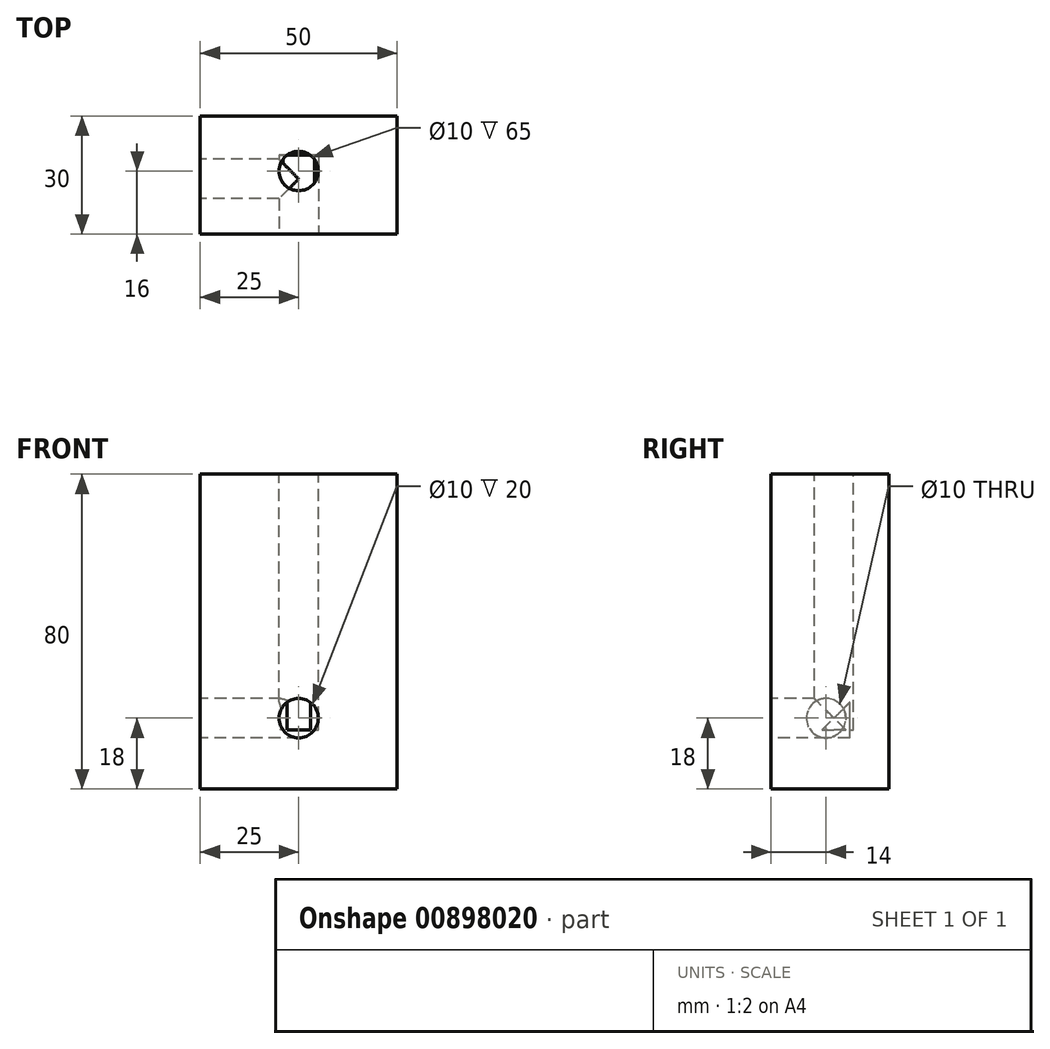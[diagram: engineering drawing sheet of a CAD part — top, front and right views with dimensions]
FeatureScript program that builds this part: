
annotation { "Feature Type Name" : "Feature", "Feature Type Description" : "" }
export const myFeature = defineFeature(function(context is Context, id is Id, definition is map)
    precondition{}
    {
        {
            var Q0;
            Q0=qCreatedBy(makeId("Front.planeOp"),FACE);
            var sketch = newSketch(context, id + "F0", { "sketchPlane" : qUnion([Q0])});
            skLineSegment(sketch, "E0.bottom", {"start": v(-25, 80) * mm, "end": v(25, 80) * mm});
            skLineSegment(sketch, "E0.top", {"start": v(-25, 0) * mm, "end": v(25, 0) * mm});
            skLineSegment(sketch, "E0.left", {"start": v(-25, 80) * mm, "end": v(-25, 0) * mm});
            skLineSegment(sketch, "E0.right", {"start": v(25, 80) * mm, "end": v(25, 0) * mm});
            skSolve(sketch);
        }
        {
            var Q0;
            Q0=makeQuery(id+"F0.imprint","IMPRINT",FACE,{"disambiguationData":[TD([[makeQuery(id+"F0.imprint","IMPRINT",EDGE,{"derivedFrom":sQuery(id+"F0.wireOp",EDGE,"E0.bottom")}),-1.0]])]});
            extrude(context, id + "F1", {"entities" : qUnion([Q0]), "depth" : 30 * mm, "offsetDistance" : 25 * mm});
        }
        {
            var Q0;
            Q0=makeQuery(id+"F1.opExtrude","CAP_FACE",FACE,{"disambiguationData":[OSD([sQuery(id+"F0.wireOp",EDGE,"E0.bottom"),sQuery(id+"F0.wireOp",EDGE,"E0.top"),sQuery(id+"F0.wireOp",EDGE,"E0.left"),sQuery(id+"F0.wireOp",EDGE,"E0.right")])],"isStart":false});
            var sketch = newSketch(context, id + "F2", { "sketchPlane" : qUnion([Q0])});
            skCircle(sketch, "E1", {"center": v(0, 18) * mm, "radius": 5 * mm});
            skSolve(sketch);
        }
        {
            var Q0;
            Q0=makeQuery(id+"F2.imprint","IMPRINT",FACE,{"disambiguationData":[TD([[makeQuery(id+"F2.imprint","IMPRINT",EDGE,{"derivedFrom":sQuery(id+"F2.wireOp",EDGE,"E1")}),1.0]])]});
            extrude(context, id + "F3", {"entities" : qUnion([Q0]), "operationType" : NewBodyOperationType.REMOVE, "oppositeDirection" : true, "depth" : 20 * mm, "offsetDistance" : 25 * mm});
        }
        {
            var Q0;
            Q0=makeQuery(id+"F1.opExtrude","SWEPT_FACE",FACE,{"disambiguationData":[OSD([sQuery(id+"F0.wireOp",EDGE,"E0.left")])]});
            var sketch = newSketch(context, id + "F4", { "sketchPlane" : qUnion([Q0])});
            skCircle(sketch, "E2", {"center": v(16, 18) * mm, "radius": 5 * mm});
            skSolve(sketch);
        }
        {
            var Q0;
            Q0 = qSketchRegion(id + "F4", true);
            extrude(context, id + "F5", {"entities" : qUnion([Q0]), "operationType" : NewBodyOperationType.REMOVE, "oppositeDirection" : true, "depth" : 25 * mm, "offsetDistance" : 25 * mm});
        }
        {
            var Q0;
            Q0=makeQuery(id+"F1.opExtrude","SWEPT_FACE",FACE,{"disambiguationData":[OSD([sQuery(id+"F0.wireOp",EDGE,"E0.bottom")])]});
            var sketch = newSketch(context, id + "F6", { "sketchPlane" : qUnion([Q0])});
            skCircle(sketch, "E3", {"center": v(0, -14) * mm, "radius": 5 * mm});
            skSolve(sketch);
        }
        {
            var Q0;
            Q0 = qSketchRegion(id + "F6", true);
            extrude(context, id + "F7", {"entities" : qUnion([Q0]), "operationType" : NewBodyOperationType.REMOVE, "oppositeDirection" : true, "depth" : 65 * mm, "offsetDistance" : 25 * mm});
        }
    });
